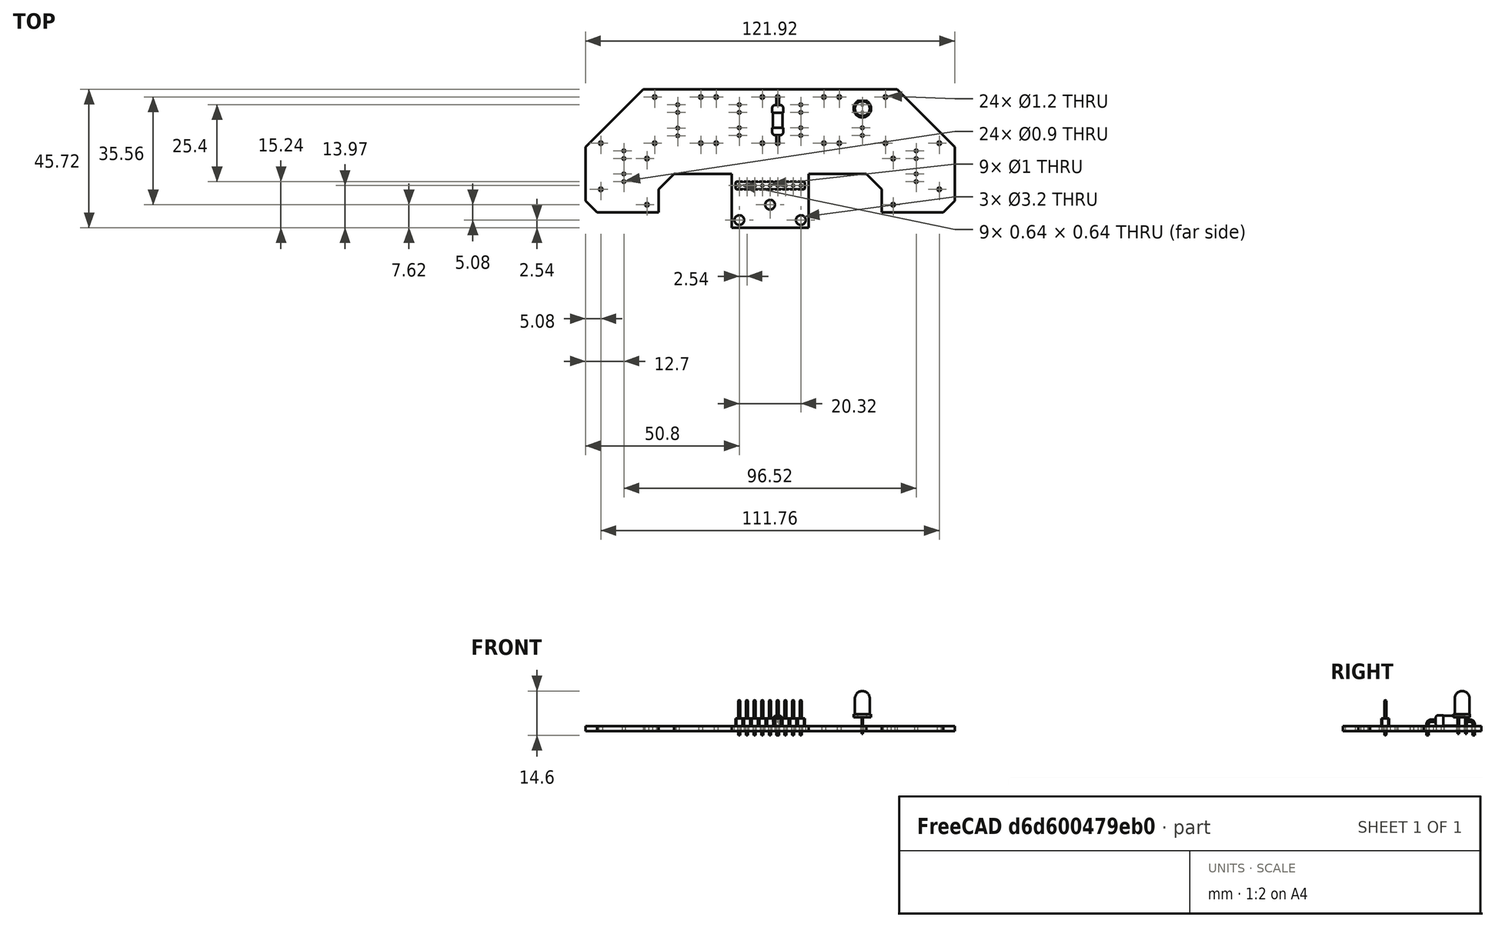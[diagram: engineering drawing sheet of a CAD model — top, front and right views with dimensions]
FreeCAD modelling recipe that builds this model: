
FCSTD DOCUMENT  (FreeCAD 0.21R33771 (Git))
Label: sensor
License: All rights reserved
LicenseURL: http://en.wikipedia.org/wiki/All_rights_reserved
objects: App::Link×22, Part::Feature×7, App::Part×4, PartDesign::CoordinateSystem×1, Sketcher::SketchObject×1
note: 9 computed .brp shape members not serialized (recipe doc carries the construction recipe); baked Part::Feature solids carry a one-line shape summary decoded from their .brp

FEATURE [PartDesign::CoordinateSystem] Local_CS_8ee6
  AttacherType = Attacher::AttachEngine3D
  MapMode = 2
  Support = -> [X_Axis001]
FEATURE [Part::Feature] Pcb_8ee6
  Placement = pos=(-119.38,76.2,0) rot=(0,0,1;0rad)
  shape: bbox 121.9 x 45.72 x 1.6 mm, 80 faces (baked)
FEATURE [Sketcher::SketchObject] PCB_Sketch_8ee6
  FullyConstrained = false
  sketch-geometry (21):
    g0: LineSegment StartX=-12.7 StartY=-3.81 StartZ=0 EndX=12.7 EndY=-3.81 EndZ=0
    g1: LineSegment StartX=12.7 StartY=-3.81 StartZ=0 EndX=12.7 EndY=13.97 EndZ=0
    g2: LineSegment StartX=12.7 StartY=13.97 StartZ=0 EndX=31.75 EndY=13.97 EndZ=0
    g3: LineSegment StartX=31.75 StartY=13.97 StartZ=0 EndX=36.83 EndY=8.89 EndZ=0
    g4: LineSegment StartX=36.83 StartY=8.89 StartZ=0 EndX=36.83 EndY=1.27 EndZ=0
    g5: LineSegment StartX=36.83 StartY=1.27 StartZ=0 EndX=57.15 EndY=1.27 EndZ=0
    g6: LineSegment StartX=57.15 StartY=1.27 StartZ=0 EndX=60.96 EndY=5.08 EndZ=0
    g7: LineSegment StartX=60.96 StartY=5.08 StartZ=0 EndX=60.96 EndY=22.86 EndZ=0
    g8: LineSegment StartX=60.96 StartY=22.86 StartZ=0 EndX=41.91 EndY=41.91 EndZ=0
    g9: LineSegment StartX=41.91 StartY=41.91 StartZ=0 EndX=-41.91 EndY=41.91 EndZ=0
    g10: LineSegment StartX=-41.91 StartY=41.91 StartZ=0 EndX=-60.96 EndY=22.86 EndZ=0
    g11: LineSegment StartX=-60.96 StartY=22.86 StartZ=0 EndX=-60.96 EndY=5.08 EndZ=0
    g12: LineSegment StartX=-60.96 StartY=5.08 StartZ=0 EndX=-57.15 EndY=1.27 EndZ=0
    g13: LineSegment StartX=-57.15 StartY=1.27 StartZ=0 EndX=-36.83 EndY=1.27 EndZ=0
    g14: LineSegment StartX=-36.83 StartY=1.27 StartZ=0 EndX=-36.83 EndY=8.89 EndZ=0
    g15: LineSegment StartX=-36.83 StartY=8.89 StartZ=0 EndX=-31.75 EndY=13.97 EndZ=0
    g16: LineSegment StartX=-31.75 StartY=13.97 StartZ=0 EndX=-12.7 EndY=13.97 EndZ=0
    g17: LineSegment StartX=-12.7 StartY=13.97 StartZ=0 EndX=-12.7 EndY=-3.81 EndZ=0
    g18: Circle CenterX=0 CenterY=3.81 CenterZ=0 NormalX=0 NormalY=0 NormalZ=1 AngleXU=0 Radius=1.6
    g19: Circle CenterX=-10.16 CenterY=-1.27 CenterZ=0 NormalX=0 NormalY=0 NormalZ=1 AngleXU=0 Radius=1.6
    g20: Circle CenterX=10.16 CenterY=-1.27 CenterZ=0 NormalX=0 NormalY=0 NormalZ=1 AngleXU=0 Radius=1.6
  constraints (18):
    c: Coincident(g11,g12)
    c: Coincident(g10,g11)
    c: Coincident(g12,g13)
    c: Coincident(g9,g10)
    c: Coincident(g13,g14)
    c: Coincident(g14,g15)
    c: Coincident(g15,g16)
    c: Coincident(g0,g17)
    c: Coincident(g16,g17)
    c: Coincident(g0,g1)
    c: Coincident(g1,g2)
    c: Coincident(g2,g3)
    c: Coincident(g4,g5)
    c: Coincident(g3,g4)
    c: Coincident(g8,g9)
    c: Coincident(g5,g6)
    c: Coincident(g6,g7)
    c: Coincident(g7,g8)
FEATURE [Part::Feature] Shape  label="schem.kicad_sch_LED_D5.0mm_6b3eedc1d47b"
  Placement = pos=(30.48,36.83,0) rot=(0,0,-1;1.5708rad)
  shape: bbox 5.8 x 5.4 x 14.1 mm, 16 faces (baked)
FEATURE [Part::Feature] Shape001  label="schem.kicad_sch_R_Axial_DIN0411_L99mm_D36mm_P1524mm_Horizontal_8e961bc54791"
  Placement = pos=(2.54,39.37,0) rot=(0,0,-1;1.5708rad)
  shape: bbox 3.897 x 16.3 x 6.748 mm, 17 faces (baked)
FEATURE [Part::Feature] Shape002  label="schem.kicad_sch_PinHeader_1x09_P254mm_Vertical_1c69e8c8ab9c"
  Placement = pos=(-10.16,10.16,0) rot=(0,0,1;1.5708rad)
  shape: bbox 22.86 x 2.54 x 11.54 mm, 220 faces (baked)
FEATURE [App::Link] schem_kicad_sch_R_Axial_DIN0411_L99mm_D36mm_P1524mm_Horizontal_8e961bc54791_ln_  label="schem.kicad_sch_sch_R_Axial_DIN0411_L99mm_D36mm_P1524mm_Horizontal_9c25d3f92c60"
  LinkPlacement = pos=(-38.1,39.37,0) rot=(0,0,-1;1.5708rad)
  LinkedObject = -> Shape001
  Placement = pos=(-38.1,39.37,0) rot=(0,0,-1;1.5708rad)
FEATURE [App::Link] schem_kicad_sch_LED_D5_0mm_6b3eedc1d47b_ln_  label="schem.kicad_sch_sch_LED_D5.0mm_e083702e349f"
  LinkPlacement = pos=(-10.16,36.83,0) rot=(0,0,-1;1.5708rad)
  LinkedObject = -> Shape
  Placement = pos=(-10.16,36.83,0) rot=(0,0,-1;1.5708rad)
FEATURE [App::Link] schem_kicad_sch_LED_D5_0mm_6b3eedc1d47b_ln_001  label="schem.kicad_sch_sch_LED_D5.0mm_62ea2af5cf7f"
  LinkPlacement = pos=(-10.16,26.67,0) rot=(0,0,1;1.5708rad)
  LinkedObject = -> Shape
  Placement = pos=(-10.16,26.67,0) rot=(0,0,1;1.5708rad)
FEATURE [App::Link] schem_kicad_sch_R_Axial_DIN0411_L99mm_D36mm_P1524mm_Horizontal_8e961bc54791_ln_001  label="schem.kicad_sch_sch_R_Axial_DIN0411_L99mm_D36mm_P1524mm_Horizontal_b18dd6d82783"
  LinkPlacement = pos=(-40.64,3.81,0) rot=(0,0,1;1.5708rad)
  LinkedObject = -> Shape001
  Placement = pos=(-40.64,3.81,0) rot=(0,0,1;1.5708rad)
FEATURE [App::Link] schem_kicad_sch_LED_D5_0mm_6b3eedc1d47b_ln_002  label="schem.kicad_sch_sch_LED_D5.0mm_0b865b62e658"
  LinkPlacement = pos=(-48.26,11.43,0) rot=(0,0,1;1.5708rad)
  LinkedObject = -> Shape
  Placement = pos=(-48.26,11.43,0) rot=(0,0,1;1.5708rad)
FEATURE [App::Link] schem_kicad_sch_LED_D5_0mm_6b3eedc1d47b_ln_003  label="schem.kicad_sch_sch_LED_D5.0mm_efbdec03e81d"
  LinkPlacement = pos=(30.48,26.67,0) rot=(0,0,1;1.5708rad)
  LinkedObject = -> Shape
  Placement = pos=(30.48,26.67,0) rot=(0,0,1;1.5708rad)
FEATURE [App::Link] schem_kicad_sch_LED_D5_0mm_6b3eedc1d47b_ln_004  label="schem.kicad_sch_sch_LED_D5.0mm_c716b53efe9b"
  LinkPlacement = pos=(48.26,11.43,0) rot=(0,0,1;1.5708rad)
  LinkedObject = -> Shape
  Placement = pos=(48.26,11.43,0) rot=(0,0,1;1.5708rad)
FEATURE [App::Link] schem_kicad_sch_R_Axial_DIN0411_L99mm_D36mm_P1524mm_Horizontal_8e961bc54791_ln_002  label="schem.kicad_sch_sch_R_Axial_DIN0411_L99mm_D36mm_P1524mm_Horizontal_53683d33316f"
  LinkPlacement = pos=(-22.86,39.37,0) rot=(0,0,-1;1.5708rad)
  LinkedObject = -> Shape001
  Placement = pos=(-22.86,39.37,0) rot=(0,0,-1;1.5708rad)
FEATURE [App::Link] schem_kicad_sch_LED_D5_0mm_6b3eedc1d47b_ln_005  label="schem.kicad_sch_sch_LED_D5.0mm_92acccb4eab0"
  LinkPlacement = pos=(10.16,36.83,0) rot=(0,0,-1;1.5708rad)
  LinkedObject = -> Shape
  Placement = pos=(10.16,36.83,0) rot=(0,0,-1;1.5708rad)
FEATURE [App::Link] schem_kicad_sch_R_Axial_DIN0411_L99mm_D36mm_P1524mm_Horizontal_8e961bc54791_ln_003  label="schem.kicad_sch_sch_R_Axial_DIN0411_L99mm_D36mm_P1524mm_Horizontal_aba21923dc87"
  LinkPlacement = pos=(-17.78,39.37,0) rot=(0,0,-1;1.5708rad)
  LinkedObject = -> Shape001
  Placement = pos=(-17.78,39.37,0) rot=(0,0,-1;1.5708rad)
FEATURE [App::Link] schem_kicad_sch_R_Axial_DIN0411_L99mm_D36mm_P1524mm_Horizontal_8e961bc54791_ln_004  label="schem.kicad_sch_sch_R_Axial_DIN0411_L99mm_D36mm_P1524mm_Horizontal_424d508a3918"
  LinkPlacement = pos=(38.1,39.37,0) rot=(0,0,-1;1.5708rad)
  LinkedObject = -> Shape001
  Placement = pos=(38.1,39.37,0) rot=(0,0,-1;1.5708rad)
FEATURE [App::Link] schem_kicad_sch_LED_D5_0mm_6b3eedc1d47b_ln_006  label="schem.kicad_sch_sch_LED_D5.0mm_5b50564bbe54"
  LinkPlacement = pos=(10.16,26.67,0) rot=(0,0,1;1.5708rad)
  LinkedObject = -> Shape
  Placement = pos=(10.16,26.67,0) rot=(0,0,1;1.5708rad)
FEATURE [App::Link] schem_kicad_sch_LED_D5_0mm_6b3eedc1d47b_ln_007  label="schem.kicad_sch_sch_LED_D5.0mm_fd8327e3986d"
  LinkPlacement = pos=(48.26,19.05,0) rot=(0,0,1;1.5708rad)
  LinkedObject = -> Shape
  Placement = pos=(48.26,19.05,0) rot=(0,0,1;1.5708rad)
FEATURE [App::Link] schem_kicad_sch_LED_D5_0mm_6b3eedc1d47b_ln_008  label="schem.kicad_sch_sch_LED_D5.0mm_a4f76ea92215"
  LinkPlacement = pos=(-48.26,19.05,0) rot=(0,0,1;1.5708rad)
  LinkedObject = -> Shape
  Placement = pos=(-48.26,19.05,0) rot=(0,0,1;1.5708rad)
FEATURE [App::Link] schem_kicad_sch_LED_D5_0mm_6b3eedc1d47b_ln_009  label="schem.kicad_sch_sch_LED_D5.0mm_9ae5ac9029b4"
  LinkPlacement = pos=(-30.48,26.59,0) rot=(0,0,1;1.5708rad)
  LinkedObject = -> Shape
  Placement = pos=(-30.48,26.59,0) rot=(0,0,1;1.5708rad)
FEATURE [App::Link] schem_kicad_sch_R_Axial_DIN0411_L99mm_D36mm_P1524mm_Horizontal_8e961bc54791_ln_005  label="schem.kicad_sch_sch_R_Axial_DIN0411_L99mm_D36mm_P1524mm_Horizontal_fadaeb29d85d"
  LinkPlacement = pos=(17.78,39.37,0) rot=(0,0,-1;1.5708rad)
  LinkedObject = -> Shape001
  Placement = pos=(17.78,39.37,0) rot=(0,0,-1;1.5708rad)
FEATURE [App::Link] schem_kicad_sch_LED_D5_0mm_6b3eedc1d47b_ln_010  label="schem.kicad_sch_sch_LED_D5.0mm_efc7ac76fd12"
  LinkPlacement = pos=(-30.48,36.83,0) rot=(0,0,-1;1.5708rad)
  LinkedObject = -> Shape
  Placement = pos=(-30.48,36.83,0) rot=(0,0,-1;1.5708rad)
FEATURE [App::Link] schem_kicad_sch_R_Axial_DIN0411_L99mm_D36mm_P1524mm_Horizontal_8e961bc54791_ln_006  label="schem.kicad_sch_sch_R_Axial_DIN0411_L99mm_D36mm_P1524mm_Horizontal_a8dc5a16b9fc"
  LinkPlacement = pos=(40.64,3.81,0) rot=(0,0,1;1.5708rad)
  LinkedObject = -> Shape001
  Placement = pos=(40.64,3.81,0) rot=(0,0,1;1.5708rad)
FEATURE [App::Link] schem_kicad_sch_R_Axial_DIN0411_L99mm_D36mm_P1524mm_Horizontal_8e961bc54791_ln_007  label="schem.kicad_sch_sch_R_Axial_DIN0411_L99mm_D36mm_P1524mm_Horizontal_96087956f354"
  LinkPlacement = pos=(22.86,39.37,0) rot=(0,0,-1;1.5708rad)
  LinkedObject = -> Shape001
  Placement = pos=(22.86,39.37,0) rot=(0,0,-1;1.5708rad)
FEATURE [App::Link] schem_kicad_sch_R_Axial_DIN0411_L99mm_D36mm_P1524mm_Horizontal_8e961bc54791_ln_008  label="schem.kicad_sch_sch_R_Axial_DIN0411_L99mm_D36mm_P1524mm_Horizontal_09902d860f3d"
  LinkPlacement = pos=(-2.54,39.37,0) rot=(0,0,-1;1.5708rad)
  LinkedObject = -> Shape001
  Placement = pos=(-2.54,39.37,0) rot=(0,0,-1;1.5708rad)
FEATURE [App::Link] schem_kicad_sch_R_Axial_DIN0411_L99mm_D36mm_P1524mm_Horizontal_8e961bc54791_ln_009  label="schem.kicad_sch_sch_R_Axial_DIN0411_L99mm_D36mm_P1524mm_Horizontal_124a3de3b5d7"
  LinkPlacement = pos=(-55.88,24.13,0) rot=(0,0,-1;1.5708rad)
  LinkedObject = -> Shape001
  Placement = pos=(-55.88,24.13,0) rot=(0,0,-1;1.5708rad)
FEATURE [App::Link] schem_kicad_sch_R_Axial_DIN0411_L99mm_D36mm_P1524mm_Horizontal_8e961bc54791_ln_010  label="schem.kicad_sch_sch_R_Axial_DIN0411_L99mm_D36mm_P1524mm_Horizontal_9fcbc7913113"
  LinkPlacement = pos=(55.88,24.13,0) rot=(0,0,-1;1.5708rad)
  LinkedObject = -> Shape001
  Placement = pos=(55.88,24.13,0) rot=(0,0,-1;1.5708rad)
FEATURE [App::Part] Top_8ee6
  Group = -> [Shape,Shape001,Shape002,schem_kicad_sch_R_Axial_DIN0411_L99mm_D36mm_P1524mm_Horizontal_8e961bc54791_ln_,schem_kicad_sch_LED_D5_0mm_6b3eedc1d47b_ln_,schem_kicad_sch_LED_D5_0mm_6b3eedc1d47b_ln_001,schem_kicad_sch_R_Axial_DIN0411_L99mm_D36mm_P1524mm_Horizontal_8e961bc54791_ln_001,schem_kicad_sch_LED_D5_0mm_6b3eedc1d47b_ln_002,schem_kicad_sch_LED_D5_0mm_6b3eedc1d47b_ln_003,+16 more]
  Origin = -> Origin003
FEATURE [App::Part] Step_Models_8ee6
  Group = -> [Top_8ee6]
  Origin = -> Origin002
FEATURE [Part::Feature] pads_area001  label="topPads_8ee6"
  Placement = pos=(-119.38,76.2,0.02) rot=(0,0,1;0rad)
  shape: bbox 114.2 x 37.96 x 2e-07 mm, 57 faces, 0 solids (baked)
FEATURE [Part::Feature] Shape004  label="topTracks_8ee6"
  Placement = pos=(-119.38,76.2,0.01) rot=(0,0,1;0rad)
  shape: bbox 118.4 x 37.16 x 2e-07 mm, 14 faces, 0 solids (baked)
FEATURE [Part::Feature] pads_area003  label="botPads_8ee6"
  Placement = pos=(-119.38,76.2,-1.62) rot=(0,0,1;0rad)
  shape: bbox 114.2 x 37.96 x 2e-07 mm, 57 faces, 0 solids (baked)
FEATURE [App::Part] Board_Geoms_8ee6
  Group = -> [Pcb_8ee6,PCB_Sketch_8ee6,pads_area001,Shape004,pads_area003]
  Origin = -> Origin
FEATURE [App::Part] Board_8ee6  label="sensor"
  Group = -> [Local_CS_8ee6,Board_Geoms_8ee6,Step_Models_8ee6]
  Origin = -> Origin001
